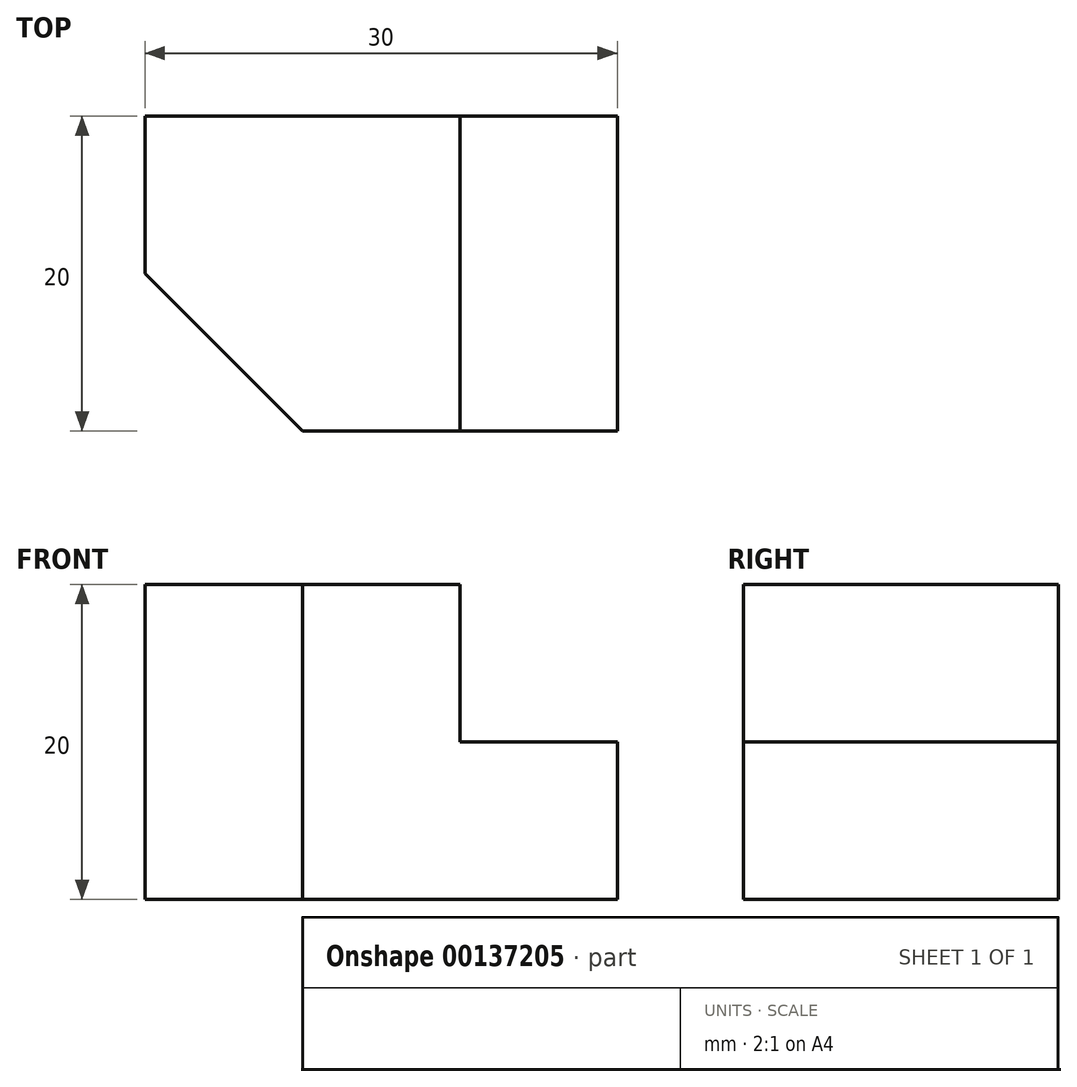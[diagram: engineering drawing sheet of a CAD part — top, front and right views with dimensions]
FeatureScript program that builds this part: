
annotation { "Feature Type Name" : "Feature", "Feature Type Description" : "" }
export const myFeature = defineFeature(function(context is Context, id is Id, definition is map)
    precondition{}
    {
        {
            var Q0;
            Q0=qCreatedBy(makeId("Front.planeOp"),FACE);
            var sketch = newSketch(context, id + "F0", { "sketchPlane" : qUnion([Q0])});
            skLineSegment(sketch, "E0", {"start": v(0, 0) * mm, "end": v(0, 20) * mm});
            skLineSegment(sketch, "E1", {"start": v(0, 20) * mm, "end": v(20, 20) * mm});
            skLineSegment(sketch, "E2", {"start": v(20, 20) * mm, "end": v(20, 10) * mm});
            skLineSegment(sketch, "E3", {"start": v(20, 10) * mm, "end": v(30, 10) * mm});
            skLineSegment(sketch, "E4", {"start": v(30, 10) * mm, "end": v(30, 0) * mm});
            skLineSegment(sketch, "E5", {"start": v(30, 0) * mm, "end": v(0, 0) * mm});
            skLineSegment(sketch, "E6", {"start": v(10, 20) * mm, "end": v(10, 0) * mm});
            skSolve(sketch);
        }
        {
            var Q0;
            Q0 = qSketchRegion(id + "F0", true);
            extrude(context, id + "F1", {"entities" : qUnion([Q0]), "depth" : 20 * mm});
        }
        {
            var Q0;
            Q0=makeQuery(id+"F1.opExtrude","SWEPT_FACE",FACE,{"disambiguationData":[OSD([sQuery(id+"F0.wireOp",EDGE,"E1")])]});
            var sketch = newSketch(context, id + "F2", { "sketchPlane" : qUnion([Q0])});
            skLineSegment(sketch, "E7", {"start": v(0, -10) * mm, "end": v(10, -20) * mm});
            skLineSegment(sketch, "E8", {"start": v(10, -20) * mm, "end": v(0, -20) * mm});
            skLineSegment(sketch, "E9", {"start": v(0, -20) * mm, "end": v(0, -10) * mm});
            skSolve(sketch);
        }
        {
            var Q0;
            Q0 = qSketchRegion(id + "F2", true);
            extrude(context, id + "F3", {"entities" : qUnion([Q0]), "operationType" : NewBodyOperationType.REMOVE, "oppositeDirection" : true, "depth" : 25 * mm});
        }
    });
